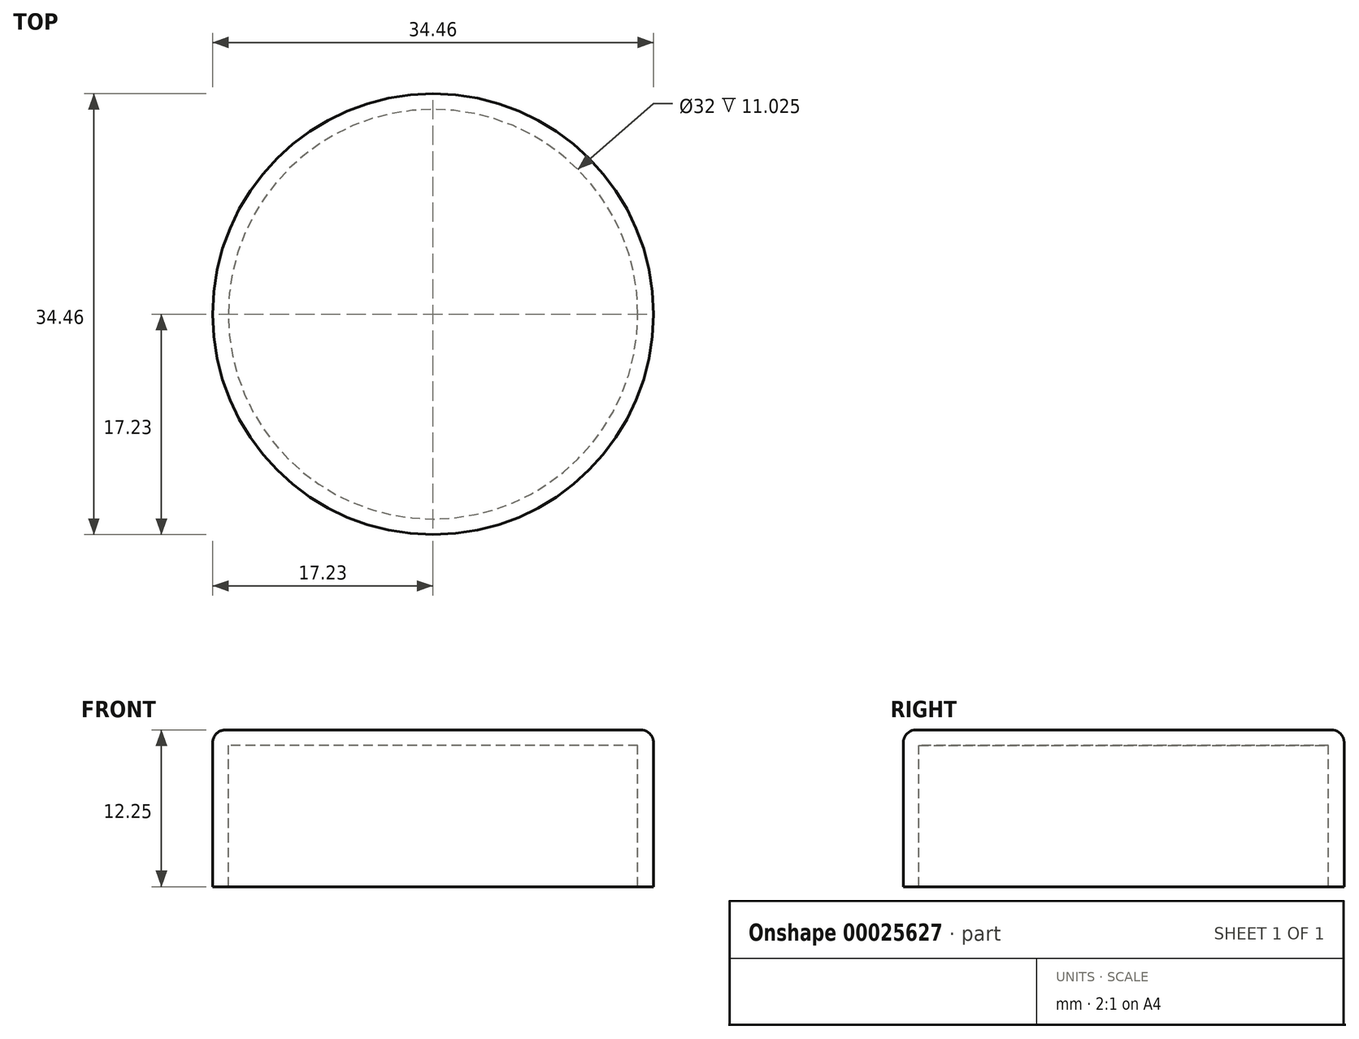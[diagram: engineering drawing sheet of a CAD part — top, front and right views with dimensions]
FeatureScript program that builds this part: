
annotation { "Feature Type Name" : "Feature", "Feature Type Description" : "" }
export const myFeature = defineFeature(function(context is Context, id is Id, definition is map)
    precondition{}
    {
        {
            var Q0;
            Q0=qCreatedBy(makeId("Front.planeOp"),FACE);
            var sketch = newSketch(context, id + "F0", { "sketchPlane" : qUnion([Q0])});
            skLineSegment(sketch, "E0.rect.bottom", {"start": v(17.23, 4.15) * mm, "end": v(0, 4.15) * mm});
            skLineSegment(sketch, "E0.rect.top", {"start": v(17.23, -8.1) * mm, "end": v(16, -8.1) * mm});
            skLineSegment(sketch, "E0.rect.left", {"start": v(17.23, 4.15) * mm, "end": v(17.23, -8.1) * mm});
            skPoint(sketch, "E0.rect.middle", {"position": v(0, 0) * mm});
            skLineSegment(sketch, "E1.0", {"start": v(16, 2.92) * mm, "end": v(16, -8.1) * mm});
            skLineSegment(sketch, "E1.1", {"start": v(16, 2.92) * mm, "end": v(0, 2.92) * mm});
            skLineSegment(sketch, "E2", {"start": v(0, 4.15) * mm, "end": v(0, 2.92) * mm});
            skSolve(sketch);
        }
        {
            var Q0;
            Q0=makeQuery(id+"F0.imprint","IMPRINT",FACE,{"disambiguationData":[TD([[makeQuery(id+"F0.imprint","IMPRINT",EDGE,{"derivedFrom":sQuery(id+"F0.wireOp",EDGE,"E0.rect.bottom")}),1.0]])]});
            var Q1;
            Q1=sQuery(id+"F0.wireOp",EDGE,"E2");
            revolve(context, id + "F1", {"entities" : qUnion([Q0]), "axis" : qUnion([Q1]), "revolveType" : RevolveType.FULL});
        }
        {
            var Q0;
            Q0=makeQuery(id+"F1.opRevolve","SWEPT_EDGE",EDGE,{"disambiguationData":[OSD([sQuery(id+"F0.wireOp",EDGE,"E0.rect.bottom"),sQuery(id+"F0.wireOp",EDGE,"E0.rect.left")])]});
            fillet(context, id + "F2", {"entities" : qUnion([Q0]), "radius" : 1 * mm, "tangentPropagation" : true, "allowEdgeOverflow" : false});
        }
    });
